# Revit family: Pump_Commercial-Sewage_Dewatering-Zoeller-X61HD_3inch_Vertical_Series
name_source: partatom
category: Mechanical Equipment
units: mm (PartAtom-declared; Revit-internal decimal feet)

## family parameters
Always vertical = No
Cut with Voids When Loaded = No
OmniClass Number = 23.60.30.21
OmniClass Title = Pumps
Part Type = Normal
Room Calculation Point = No
Round Connector Dimension = Use Radius
Shared = Yes
Work Plane-Based = Yes

## types (42) — shared parameters
Assembly Code = D2090
Cord Length (Optional) = 600"
Default Elevation = 0"
Description = Solid Handling Pump With Explosion Proof Motor, For Hazardous Location
Discharge Description = 3in NPT Vertical Discharge
Discharge Diameter = 3"
Discharge Radius = 1 1/2"
Flange = ANSI B16.1
Height = 33 1/4"
Hertz = 60
Impeller Type (Optional) = Ductile Iron Vortex or Bronze Semi-Open
Installation Type = Floor Mounted
Inverter Duty Submersible (1-5 BHP Only) = No
Lead Wires Insulation = Class F
Length = 17 9/16"
Manufacturer = Zoeller
Material = Cast Iron-Zoeller-Powder Coated Epoxy
Max. Stator Temp. = 311 °F
Max. Water Temp. = 104 °F
Mechanical Seals = Tandem carbon/ceramic upper and silicon carbide/silicon carbide lower
Min. Recommended Fluid Level = 24"
Moisture Detection = Moisture Sensing Probes (Requires a circuit in control panel)
Motor Design Letter = NEMA B
Motor Shaft = 416 S.S.
Motor Type = Submersible Explosion Proof
O-Rings (Optional) Viton = No
O-Rings Seals = Buna-N
Operation = Non-Automatic
Power Cord = #12-4 SO(Models with a FLA greater than 20 amps use #8-4 gauge power cord.) / #18-5 SO(Requires a circuit in control panel to function)
Price = Prices may vary. Please consult Manufacturer Representative for most up-to-date price list.
Product Documentation Link = http://cdn.qleapahead.com
Product Page URL = http://www.zoellerengprod.com
Shaft Seal (Standard) = Carbon/Ceramic
Shaft Seal Lower (Options) = Carbon/Silicon Carbide, Silicon Carbide/Silicon Carbide
Shaft Seal Upper (Options) = Carbon/Silicon Carbide, Silicon Carbide/Silicon Carbide
Solid Size = 2-1/2" (64mm)
Solid Size (Optional) 3" = No
Tandem Seals = Standard
Type SOW Power Cord Length = 300"
URL = http://www.zoellerengprod.com
Warranty Information = 15 Months Limited Warranty
Waste Connection = Yes
Width = 12 5/8"

## per-type parameters (varying)
| type | Amps | Apparent Load | Flow @ 5' | Impeller Diameter | Impeller Type | Locked Rotor Amps (Voltage Dependant) | Max. Head | Maximum KW Input | Model | Motor | Motor Thermal Shutoff | NEC Locked Rotor Code | Phase | RPM | Service Factor | Shipping Weight | Voltage |
| X6120-230V/1Ph/6.9A/1HP | 7 A | 1587 VA | 250 GPM | 4 7/8" | Ductile Iron Semi-open | 48 | 22' | 1.4 | X6120 | 1 HP | Thermal Sensors (Requires a circuit in control panel) | M | 1 | 1750 | 1.2 | 295 lbs (134 kg) | 230 V |
| X6120-200V/3Ph/4.8A/1HP | 5 A | 960 VA | 250 GPM | 4 7/8" | Ductile Iron Semi-open | 32 | 22' | 1.4 | X6120 | 1 HP | Thermal Sensors (Requires a circuit in control panel) | M | 3 | 1750 | 1.2 | 295 lbs (134 kg) | 200 V |
| X6120-230V/3Ph/4.2A/1HP | 4 A | 966 VA | 250 GPM | 4 7/8" | Ductile Iron Semi-open | 28 | 22' | 1.4 | X6120 | 1 HP | Thermal Sensors (Requires a circuit in control panel) | M | 3 | 1750 | 1.2 | 295 lbs (134 kg) | 230 V |
| X6120-460V/3Ph/2.1A/1HP | 2 A | 966 VA | 250 GPM | 4 7/8" | Ductile Iron Semi-open | 14 | 22' | 1.4 | X6120 | 1 HP | Thermal Sensors (Requires a circuit in control panel) | M | 3 | 1750 | 1.2 | 295 lbs (134 kg) | 460 V |
| X6120-575V/3Ph/1.7A/1HP | 2 A | 978 VA | 250 GPM | 4 7/8" | Ductile Iron Semi-open | 11.5 | 22' | 1.4 | X6120 | 1 HP | Thermal Sensors (Requires a circuit in control panel) | M | 3 | 1750 | 1.2 | 295 lbs (134 kg) | 575 V |
| X6121-230V/1Ph/8.9A/1.5HP | 9 A | 2047 VA | 320 GPM | 5 3/8" | Ductile Iron Semi-open | 48 | 29' | 1.9 | X6121 | 1.5 HP | Thermal Sensors (Requires a circuit in control panel) | J | 1 | 1750 | 1.2 | 295 lbs (134 kg) | 230 V |
| X6121-200V/3Ph/5.9A/1.5HP | 6 A | 1180 VA | 320 GPM | 5 3/8" | Ductile Iron Semi-open | 32 | 29' | 1.9 | X6121 | 1.5 HP | Thermal Sensors (Requires a circuit in control panel) | J | 3 | 1750 | 1.2 | 295 lbs (134 kg) | 200 V |
| X6121-230V/3Ph/5.1A/1.5HP | 5 A | 1173 VA | 320 GPM | 5 3/8" | Ductile Iron Semi-open | 28 | 29' | 1.9 | X6121 | 1.5 HP | Thermal Sensors (Requires a circuit in control panel) | J | 3 | 1750 | 1.2 | 295 lbs (134 kg) | 230 V |
| X6121-460V/3Ph/2.6A/1.5HP | 3 A | 1196 VA | 320 GPM | 5 3/8" | Ductile Iron Semi-open | 14 | 29' | 1.9 | X6121 | 1.5 HP | Thermal Sensors (Requires a circuit in control panel) | J | 3 | 1750 | 1.2 | 295 lbs (134 kg) | 460 V |
| X6121-575V/3Ph/2.0A/1.5HP | 2 A | 1150 VA | 320 GPM | 5 3/8" | Ductile Iron Semi-open | 11.5 | 29' | 1.9 | X6121 | 1.5 HP | Thermal Sensors (Requires a circuit in control panel) | J | 3 | 1750 | 1.2 | 295 lbs (134 kg) | 575 V |
| X6122-230V/1Ph/14.5A/2HP | 15 A | 3335 VA | 380 GPM | 5 3/4" | Ductile Iron Semi-open | 86 | 35' | 2.4 | X6122 | 2 HP | Thermal Sensors (Requires a circuit in control panel) | K | 1 | 1750 | 1.2 | 295 lbs (134 kg) | 230 V |
| X6122-200V/3Ph/7.8A/2HP | 8 A | 1560 VA | 380 GPM | 5 3/4" | Ductile Iron Semi-open | 46 | 35' | 2.4 | X6122 | 2 HP | Thermal Sensors (Requires a circuit in control panel) | K | 3 | 1750 | 1.2 | 295 lbs (134 kg) | 200 V |
| X6122-230V/3Ph/6.8A/2HP | 7 A | 1564 VA | 380 GPM | 5 3/4" | Ductile Iron Semi-open | 41 | 35' | 2.4 | X6122 | 2 HP | Thermal Sensors (Requires a circuit in control panel) | K | 3 | 1750 | 1.2 | 295 lbs (134 kg) | 230 V |
| X6122-460V/3Ph/3.4A/2HP | 3 A | 1564 VA | 380 GPM | 5 3/4" | Ductile Iron Semi-open | 20.5 | 35' | 2.4 | X6122 | 2 HP | Thermal Sensors (Requires a circuit in control panel) | K | 3 | 1750 | 1.2 | 295 lbs (134 kg) | 460 V |
| X6122-575V/3Ph/2.7A/2HP | 3 A | 1553 VA | 380 GPM | 5 3/4" | Ductile Iron Semi-open | 16.2 | 35' | 2.4 | X6122 | 2 HP | Thermal Sensors (Requires a circuit in control panel) | K | 3 | 1750 | 1.2 | 295 lbs (134 kg) | 575 V |
| X6123-230V/1Ph/17.0A/3HP | 17 A | 3910 VA | 450 GPM | 6 3/8" | Ductile Iron Semi-open | 86 | 44' | 3.5 | X6123 | 3 HP | Thermal Sensors (Requires a circuit in control panel) | F | 1 | 1750 | 1.2 | 295 lbs (134 kg) | 230 V |
| X6123-200V/3Ph/11.0A/3HP | 11 A | 2200 VA | 450 GPM | 6 3/8" | Ductile Iron Semi-open | 46 | 44' | 3.5 | X6123 | 3 HP | Thermal Sensors (Requires a circuit in control panel) | F | 3 | 1750 | 1.2 | 295 lbs (134 kg) | 200 V |
| X6123-230V/3Ph/9.6A/3HP | 10 A | 2208 VA | 450 GPM | 6 3/8" | Ductile Iron Semi-open | 41 | 44' | 3.5 | X6123 | 3 HP | Thermal Sensors (Requires a circuit in control panel) | F | 3 | 1750 | 1.2 | 295 lbs (134 kg) | 230 V |
| X6123-460V/3Ph/4.8A/3HP | 5 A | 2208 VA | 450 GPM | 6 3/8" | Ductile Iron Semi-open | 20.5 | 44' | 3.5 | X6123 | 3 HP | Thermal Sensors (Requires a circuit in control panel) | F | 3 | 1750 | 1.2 | 295 lbs (134 kg) | 460 V |
| X6123-575V/3Ph/3.9A/3HP | 4 A | 2243 VA | 450 GPM | 6 3/8" | Ductile Iron Semi-open | 16.2 | 44' | 3.5 | X6123 | 3 HP | Thermal Sensors (Requires a circuit in control panel) | F | 3 | 1750 | 1.2 | 295 lbs (134 kg) | 575 V |
| X6124-230V/1Ph/28.0A/5HP | 28 A | 6440 VA | 535 GPM | 7" | Ductile Iron Semi-open | 139 | 54' | 5.5 | X6124 | 5 HP | Thermal Sensors (Requires a circuit in control panel) | E | 1 | 1750 | 1.2 | 295 lbs (134 kg) | 230 V |
| X6124-200V/3Ph/17.5A/5HP | 18 A | 3500 VA | 535 GPM | 7" | Ductile Iron Semi-open | 64 | 54' | 5.5 | X6124 | 5 HP | Thermal Sensors (Requires a circuit in control panel) | E | 3 | 1750 | 1.2 | 295 lbs (134 kg) | 200 V |
| X6124-230V/3Ph/15.2A/5HP | 15 A | 3496 VA | 535 GPM | 7" | Ductile Iron Semi-open | 58 | 54' | 5.5 | X6124 | 5 HP | Thermal Sensors (Requires a circuit in control panel) | E | 3 | 1750 | 1.2 | 295 lbs (134 kg) | 230 V |
| X6124-460V/3Ph/7.6A/5HP | 8 A | 3496 VA | 535 GPM | 7" | Ductile Iron Semi-open | 29 | 54' | 5.5 | X6124 | 5 HP | Thermal Sensors (Requires a circuit in control panel) | E | 3 | 1750 | 1.2 | 295 lbs (134 kg) | 460 V |
| X6124-575V/3Ph/6.1A/5HP | 6 A | 3508 VA | 535 GPM | 7" | Ductile Iron Semi-open | 23 | 54' | 5.5 | X6124 | 5 HP | Thermal Sensors (Requires a circuit in control panel) | E | 3 | 1750 | 1.2 | 295 lbs (134 kg) | 575 V |
| X6125-200V/3Ph/25.3A/7.5HP | 25 A | 5060 VA | 600 GPM | 7 1/2" | Ductile Iron Semi-open | 83 | 65' | 6.9 | X6125 | 7.5 HP | Thermal Sensors (Requires a circuit in control panel) | C | 3 | 1750 | 1 | 295 lbs (134 kg) | 200 V |
| X6125-230V/3Ph/22.0A/7.5HP | 22 A | 5060 VA | 600 GPM | 7 1/2" | Ductile Iron Semi-open | 72.0 | 65' | 6.9 | X6125 | 7.5 HP | Thermal Sensors (Requires a circuit in control panel) | C | 3 | 1750 | 1 | 295 lbs (134 kg) | 230 V |
| X6125-460V/3Ph/11.0A/7.5HP | 11 A | 5060 VA | 600 GPM | 7 1/2" | Ductile Iron Semi-open | 36 | 65' | 6.9 | X6125 | 7.5 HP | Thermal Sensors (Requires a circuit in control panel) | C | 3 | 1750 | 1 | 295 lbs (134 kg) | 460 V |
| X6125-575V/3Ph/9.0A/7.5HP | 9 A | 5175 VA | 600 GPM | 7 1/2" | Ductile Iron Semi-open | 29.0 | 65' | 6.9 | X6125 | 7.5 HP | Thermal Sensors (Requires a circuit in control panel) | C | 3 | 1750 | 1 | 295 lbs (134 kg) | 575 V |
| X6111-230V/1Ph/28.0A/5HP | 28 A | 6440 VA | 470 GPM | 4 3/8" | Bronze Semi-Open | 132 | 65' | 5.3 | X6111 | 5 HP | Thermal Sensors With Automatic Reset (Requires a circuit in control panel) | E | 1 | 3450 | 1.2 | 245 lbs (111 kg) | 230 V |
| X6111-200V/3Ph/17.5A/5HP | 18 A | 3500 VA | 470 GPM | 4 3/8" | Bronze Semi-Open | 66.0 | 65' | 5.3 | X6111 | 5 HP | Thermal Sensors With Automatic Reset (Requires a circuit in control panel) | E | 3 | 3450 | 1.2 | 245 lbs (111 kg) | 200 V |
| X6111-230V/3Ph/15.2A/5HP | 15 A | 3496 VA | 470 GPM | 4 3/8" | Bronze Semi-Open | 57.0 | 65' | 5.3 | X6111 | 5 HP | Thermal Sensors With Automatic Reset (Requires a circuit in control panel) | E | 3 | 3450 | 1.2 | 245 lbs (111 kg) | 230 V |
| X6111-460V/3Ph/7.6A/5HP | 8 A | 3496 VA | 470 GPM | 4 3/8" | Bronze Semi-Open | 28.5 | 65' | 5.3 | X6111 | 5 HP | Thermal Sensors With Automatic Reset (Requires a circuit in control panel) | E | 3 | 3450 | 1.2 | 245 lbs (111 kg) | 460 V |
| X6111-575V/3Ph/6.1A/5HP | 6 A | 3508 VA | 470 GPM | 4 3/8" | Bronze Semi-Open | 25.2 | 65' | 5.3 | X6111 | 5 HP | Thermal Sensors With Automatic Reset (Requires a circuit in control panel) | E | 3 | 3450 | 1.2 | 245 lbs (111 kg) | 575 V |
| X6112-200V/3Ph/25.3A/7.5HP | 25 A | 5060 VA | 550 GPM | 4 3/4" | Bronze Semi-Open | 94.0 | 82' | 7.8 | X6112 | 7.5 HP | Thermal Sensors With Automatic Reset (Requires a circuit in control panel) | D | 3 | 3450 | 1.2 | 245 lbs (111 kg) | 200 V |
| X6112-230V/3Ph/22.0A/7.5HP | 22 A | 5060 VA | 550 GPM | 4 3/4" | Bronze Semi-Open | 82.0 | 82' | 7.8 | X6112 | 7.5 HP | Thermal Sensors With Automatic Reset (Requires a circuit in control panel) | D | 3 | 3450 | 1.2 | 245 lbs (111 kg) | 230 V |
| X6112-460V/3Ph/11.0A/7.5HP | 11 A | 5060 VA | 550 GPM | 4 3/4" | Bronze Semi-Open | 41.0 | 82' | 7.8 | X6112 | 7.5 HP | Thermal Sensors With Automatic Reset (Requires a circuit in control panel) | D | 3 | 3450 | 1.2 | 245 lbs (111 kg) | 460 V |
| X6112-575V/3Ph/9.0A/7.5HP | 9 A | 5175 VA | 550 GPM | 4 3/4" | Bronze Semi-Open | 36.0 | 82' | 7.8 | X6112 | 7.5 HP | Thermal Sensors With Automatic Reset (Requires a circuit in control panel) | D | 3 | 3450 | 1.2 | 245 lbs (111 kg) | 575 V |
| X6113-200V/3Ph/32.2A/10HP | 32 A | 6440 VA | 620 GPM | 5 1/8" | Bronze Semi-Open | 94.0 | 106' | 10.5 | X6113 | 10 HP | Thermal Sensors With Automatic Reset (Requires a circuit in control panel) | B | 3 | 3450 | 1 | 245 lbs (111 kg) | 200 V |
| X6113-230V/3Ph/28.0A/10HP | 28 A | 6440 VA | 620 GPM | 5 1/8" | Bronze Semi-Open | 82.0 | 106' | 10.5 | X6113 | 10 HP | Thermal Sensors With Automatic Reset (Requires a circuit in control panel) | B | 3 | 3450 | 1 | 245 lbs (111 kg) | 230 V |
| X6113-460V/3Ph/14.0A/10HP | 14 A | 6440 VA | 620 GPM | 5 1/8" | Bronze Semi-Open | 41.0 | 106' | 10.5 | X6113 | 10 HP | Thermal Sensors With Automatic Reset (Requires a circuit in control panel) | B | 3 | 3450 | 1 | 245 lbs (111 kg) | 460 V |
| X6113-575V/3Ph/11.0A/10HP | 11 A | 6325 VA | 620 GPM | 5 1/8" | Bronze Semi-Open | 36.0 | 106' | 10.5 | X6113 | 10 HP | Thermal Sensors With Automatic Reset (Requires a circuit in control panel) | B | 3 | 3450 | 1 | 245 lbs (111 kg) | 575 V |

## geometry (parser evidence)
native form markers: Blend x4, Sweep x1
no freeform markers — native parametric forms only
